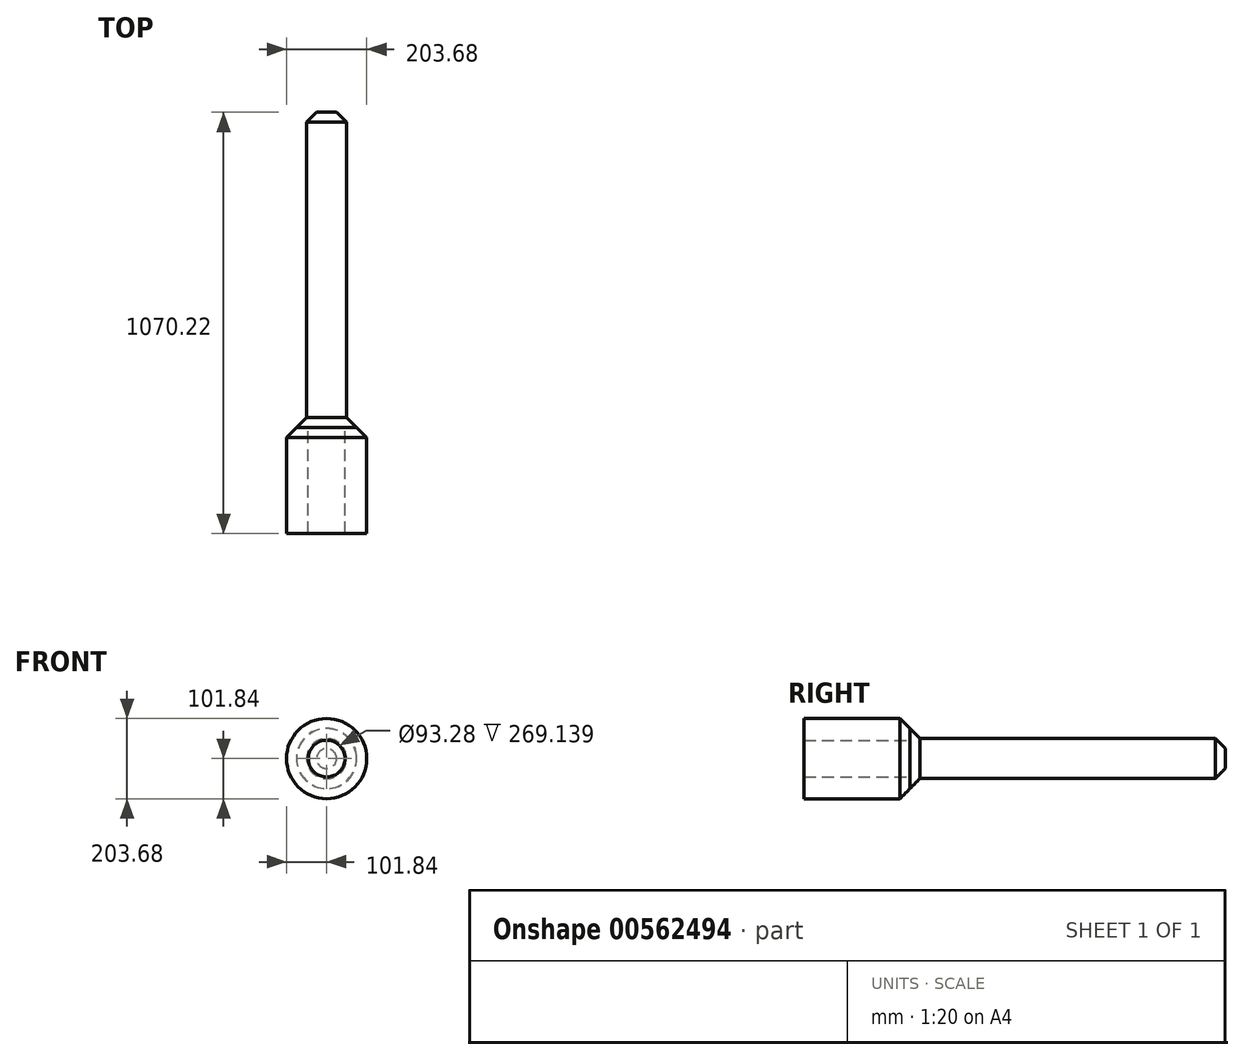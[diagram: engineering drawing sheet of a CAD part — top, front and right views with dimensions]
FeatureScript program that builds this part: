
annotation { "Feature Type Name" : "Feature", "Feature Type Description" : "" }
export const myFeature = defineFeature(function(context is Context, id is Id, definition is map)
    precondition{}
    {
        {
            var Q0;
            Q0=qCreatedBy(makeId("Front.planeOp"),FACE);
            var sketch = newSketch(context, id + "F0", { "sketchPlane" : qUnion([Q0])});
            skCircle(sketch, "E0", {"center": v(0, 0) * mm, "radius": 101.84 * mm});
            skCircle(sketch, "E1", {"center": v(0, 0) * mm, "radius": 46.64 * mm});
            skSolve(sketch);
        }
        {
            var Q0;
            Q0=makeQuery(id+"F0.imprint","IMPRINT",FACE,{"disambiguationData":[TD([[makeQuery(id+"F0.imprint","IMPRINT",EDGE,{"derivedFrom":sQuery(id+"F0.wireOp",EDGE,"E0")}),1.0]])]});
            extrude(context, id + "F1", {"entities" : qUnion([Q0]), "depth" : 269.14 * mm, "offsetDistance" : 25.4 * mm});
        }
        {
            var Q0;
            Q0=qCreatedBy(makeId("Front.planeOp"),FACE);
            var sketch = newSketch(context, id + "F2", { "sketchPlane" : qUnion([Q0])});
            skCircle(sketch, "E2", {"center": v(0, 0) * mm, "radius": 50.78 * mm});
            skSolve(sketch);
        }
        {
            var Q0;
            Q0=makeQuery(id+"F2.imprint","IMPRINT",FACE,{"disambiguationData":[TD([[makeQuery(id+"F2.imprint","IMPRINT",EDGE,{"derivedFrom":sQuery(id+"F2.wireOp",EDGE,"E2")}),1.0]])]});
            extrude(context, id + "F3", {"entities" : qUnion([Q0]), "operationType" : NewBodyOperationType.ADD, "oppositeDirection" : true, "depth" : 801.08 * mm, "offsetDistance" : 25.4 * mm});
        }
        {
            var Q0;
            Q0=makeQuery(id+"F3.opExtrude","SWEPT_FACE",FACE,{"disambiguationData":[OSD([sQuery(id+"F2.wireOp",EDGE,"E2")])]});
            var Q1;
            Q1=makeQuery(id+"F1.opExtrude","CAP_EDGE",EDGE,{"disambiguationData":[OSD([sQuery(id+"F0.wireOp",EDGE,"E0")])],"isStart":true});
            chamfer(context, id + "F4", {"entities" : qUnion([Q0, Q1]), "width" : 25.4 * mm, "tangentPropagation" : true});
        }
    });
